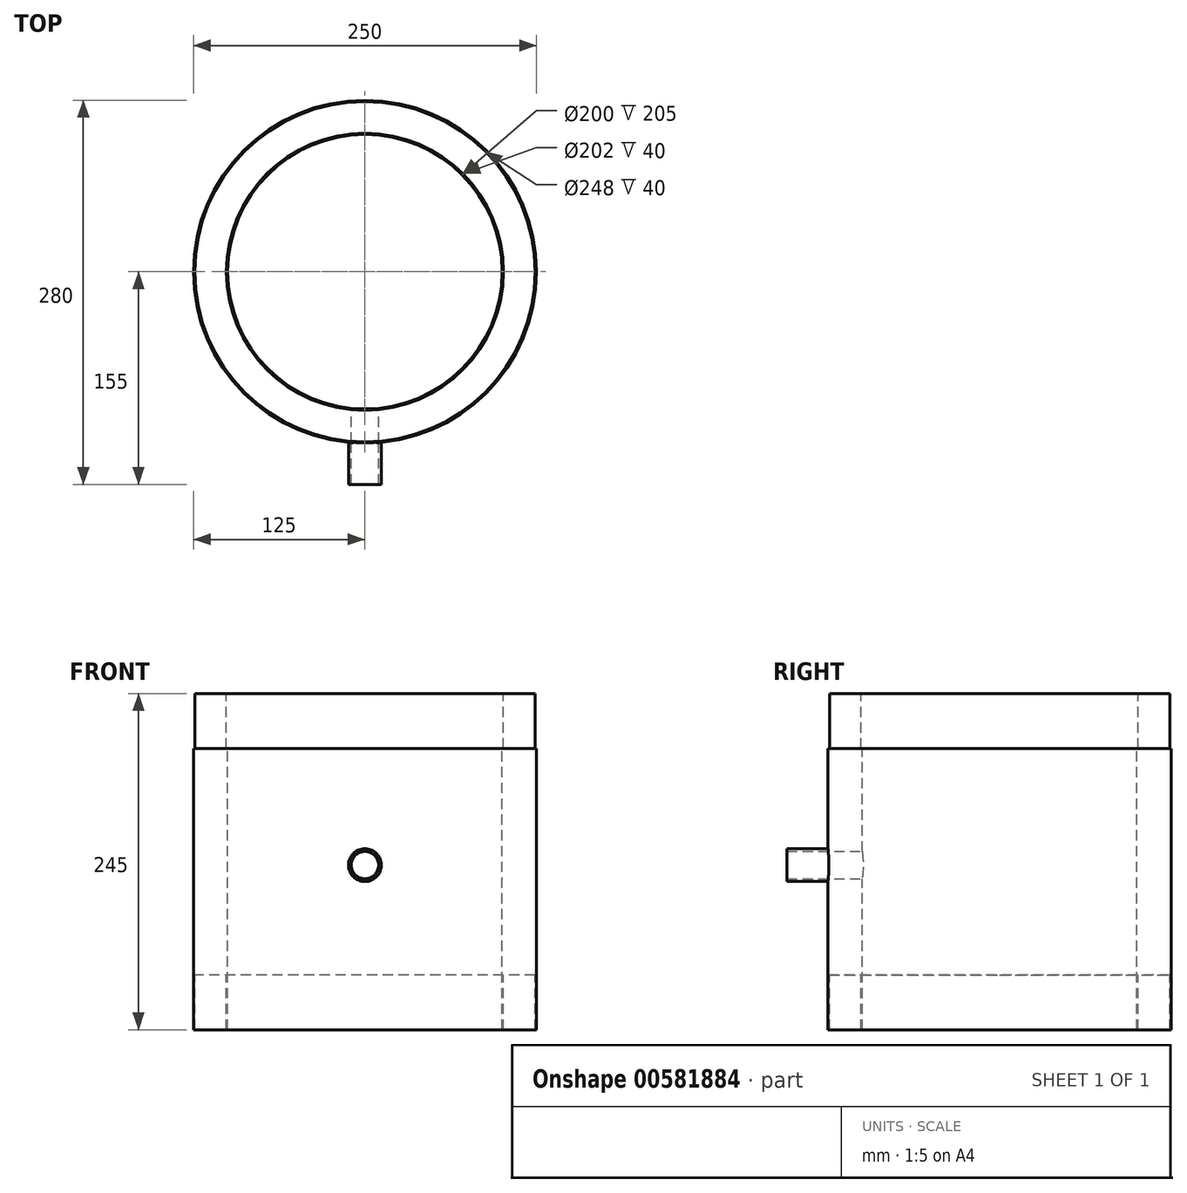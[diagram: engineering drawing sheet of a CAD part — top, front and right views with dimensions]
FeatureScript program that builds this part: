
annotation { "Feature Type Name" : "Feature", "Feature Type Description" : "" }
export const myFeature = defineFeature(function(context is Context, id is Id, definition is map)
    precondition{}
    {
        {
            var Q0;
            Q0=qCreatedBy(makeId("Front.planeOp"),FACE);
            var sketch = newSketch(context, id + "F0", { "sketchPlane" : qUnion([Q0])});
            skLineSegment(sketch, "E0", {"start": v(0, 74.87) * mm, "end": v(0, -73.71) * mm, "construction": true});
            skLineSegment(sketch, "E1", {"start": v(0, 374.84) * mm, "end": v(0, -528.94) * mm, "construction": true});
            skLineSegment(sketch, "E2", {"start": v(-100, -489.75) * mm, "end": v(-100, -284.75) * mm});
            skLineSegment(sketch, "E3", {"start": v(-100, -284.75) * mm, "end": v(-101, -284.75) * mm});
            skLineSegment(sketch, "E4", {"start": v(-101, -284.75) * mm, "end": v(-101, -244.75) * mm});
            skLineSegment(sketch, "E5", {"start": v(-101, -244.75) * mm, "end": v(-124, -244.75) * mm});
            skLineSegment(sketch, "E6", {"start": v(-124, -244.75) * mm, "end": v(-124, -284.75) * mm});
            skLineSegment(sketch, "E7", {"start": v(-124, -284.75) * mm, "end": v(-125, -284.75) * mm});
            skLineSegment(sketch, "E8", {"start": v(-125, -284.75) * mm, "end": v(-125, -489.75) * mm});
            skLineSegment(sketch, "E9", {"start": v(-125, -489.75) * mm, "end": v(-124, -489.75) * mm});
            skLineSegment(sketch, "E10", {"start": v(-124, -489.75) * mm, "end": v(-124, -449.75) * mm});
            skLineSegment(sketch, "E11", {"start": v(-124, -449.75) * mm, "end": v(-101, -449.75) * mm});
            skLineSegment(sketch, "E12", {"start": v(-101, -449.75) * mm, "end": v(-101, -489.75) * mm});
            skLineSegment(sketch, "E13", {"start": v(-101, -489.75) * mm, "end": v(-100, -489.75) * mm});
            skSolve(sketch);
        }
        {
            var Q0;
            Q0=qSketchRegion(id+"F0",true);
            var Q1;
            Q1=sQuery(id+"F0.wireOp",EDGE,"E1");
            revolve(context, id + "F1", {"entities" : qUnion([Q0]), "axis" : qUnion([Q1]), "revolveType" : RevolveType.FULL});
        }
        {
            var Q0;
            Q0=qCreatedBy(makeId("Front.planeOp"),FACE);
            var sketch = newSketch(context, id + "F2", { "sketchPlane" : qUnion([Q0])});
            skLineSegment(sketch, "E14", {"start": v(0, 0) * mm, "end": v(0, -739.5) * mm, "construction": true});
            skCircle(sketch, "E15", {"center": v(0, -369.75) * mm, "radius": 10 * mm});
            skLineSegment(sketch, "E16.0", {"start": v(-124, -244.75) * mm, "end": v(124, -244.75) * mm, "construction": true});
            skSolve(sketch);
        }
        {
            var Q0;
            Q0=qSketchRegion(id+"F2",true);
            extrude(context, id + "F3", {"entities" : qUnion([Q0]), "operationType" : NewBodyOperationType.REMOVE, "offsetDistance" : 25 * mm, "depth" : 387 * mm});
        }
        {
            var Q0;
            Q0=qCreatedBy(makeId("Front.planeOp"),FACE);
            cPlane(context, id + "F4", {"entities" : qUnion([Q0]), "cplaneType" : CPlaneType.OFFSET, "offset" : 105 * mm, "width" : 150 * mm, "height" : 150 * mm});
        }
        {
            var Q0;
            Q0=qCreatedBy(id+"F4.planeOp",FACE);
            var sketch = newSketch(context, id + "F5", { "sketchPlane" : qUnion([Q0])});
            skLineSegment(sketch, "E17", {"start": v(0, 0) * mm, "end": v(0, -620.93) * mm, "construction": true});
            skLineSegment(sketch, "E18.0", {"start": v(-124, -244.75) * mm, "end": v(124, -244.75) * mm, "construction": true});
            skCircle(sketch, "E19.0", {"center": v(0, -369.75) * mm, "radius": 10 * mm});
            skCircle(sketch, "E20", {"center": v(0, -369.75) * mm, "radius": 12 * mm});
            skSolve(sketch);
        }
        {
            var Q0;
            Q0=qSketchRegion(id+"F5",true);
            extrude(context, id + "F6", {"entities" : qUnion([Q0]), "operationType" : NewBodyOperationType.ADD, "depth" : 50 * mm, "offsetDistance" : 25 * mm});
        }
    });
